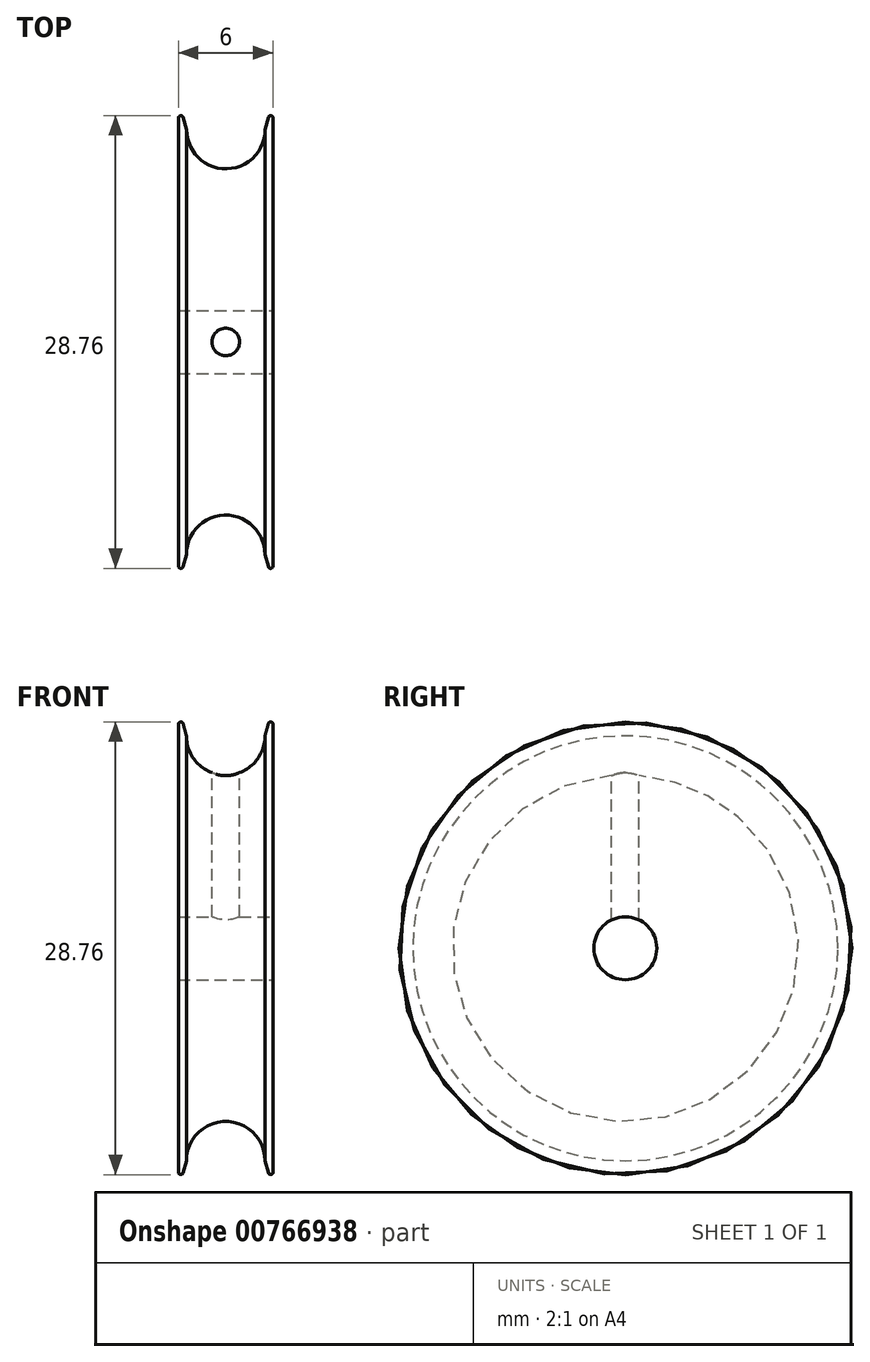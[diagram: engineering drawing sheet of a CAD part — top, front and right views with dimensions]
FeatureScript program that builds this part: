
annotation { "Feature Type Name" : "Feature", "Feature Type Description" : "" }
export const myFeature = defineFeature(function(context is Context, id is Id, definition is map)
    precondition{}
    {
        {
            var Q0;
            Q0=qCreatedBy(makeId("Front.planeOp"),FACE);
            var sketch = newSketch(context, id + "F0", { "sketchPlane" : qUnion([Q0])});
            skArc(sketch, "E0", {"start": v(-2.5, 13.5) * mm, "mid": v(0, 11) * mm, "end": v(2.5, 13.5) * mm});
            skLineSegment(sketch, "E1", {"start": v(2.5, 13.5) * mm, "end": v(2.5, 0) * mm, "construction": true});
            skLineSegment(sketch, "E2", {"start": v(-2.5, 13.5) * mm, "end": v(-2.5, 0) * mm, "construction": true});
            skLineSegment(sketch, "E3", {"start": v(2.5, 13.5) * mm, "end": v(3, 13.5) * mm, "construction": true});
            skLineSegment(sketch, "E4", {"start": v(3, 13.5) * mm, "end": v(3, 0) * mm});
            skLineSegment(sketch, "E5", {"start": v(-2.5, 13.5) * mm, "end": v(-3, 13.5) * mm, "construction": true});
            skLineSegment(sketch, "E6", {"start": v(-3, 13.5) * mm, "end": v(-3, 0) * mm});
            skLineSegment(sketch, "E7", {"start": v(-3, 0) * mm, "end": v(3, 0) * mm});
            skLineSegment(sketch, "E8", {"start": v(-2.5, 13.5) * mm, "end": v(-3, 15.37) * mm});
            skLineSegment(sketch, "E9", {"start": v(-3, 13.5) * mm, "end": v(-3, 15.37) * mm});
            skLineSegment(sketch, "E10.MirrorCS", {"start": v(2.5, 13.5) * mm, "end": v(3, 15.37) * mm});
            skLineSegment(sketch, "E11.MirrorCS", {"start": v(3, 13.5) * mm, "end": v(3, 15.37) * mm});
            skSolve(sketch);
        }
        {
            var Q0;
            Q0=makeQuery(id+"F0.imprint","IMPRINT",FACE,{"disambiguationData":[TD([[makeQuery(id+"F0.imprint","IMPRINT",EDGE,{"derivedFrom":sQuery(id+"F0.wireOp",EDGE,"E0")}),-1.0]])]});
            var Q1;
            Q1=sQuery(id+"F0.wireOp",EDGE,"E7");
            revolve(context, id + "F1", {"surfaceOperationType" : NewSurfaceOperationType.NEW, "entities" : qUnion([Q0]), "axis" : qUnion([Q1]), "revolveType" : RevolveType.FULL});
        }
        {
            var Q0;
            Q0=makeQuery(id+"F1.opRevolve","SWEPT_EDGE",EDGE,{"disambiguationData":[OSD([sQuery(id+"F0.wireOp",EDGE,"E8"),sQuery(id+"F0.wireOp",EDGE,"E9")])]});
            var Q1;
            Q1=makeQuery(id+"F1.opRevolve","SWEPT_EDGE",EDGE,{"disambiguationData":[OSD([sQuery(id+"F0.wireOp",EDGE,"E10.MirrorCS"),sQuery(id+"F0.wireOp",EDGE,"E11.MirrorCS")])]});
            fillet(context, id + "F2", {"entities" : qUnion([Q0, Q1]), "radius" : .15 * mm, "tangentPropagation" : true, "allowEdgeOverflow" : false});
        }
        {
            var Q0;
            Q0=makeQuery(id+"F1.opRevolve","SWEPT_FACE",FACE,{"disambiguationData":[OSD([sQuery(id+"F0.wireOp",EDGE,"E4")])]});
            var sketch = newSketch(context, id + "F3", { "sketchPlane" : qUnion([Q0])});
            skPoint(sketch, "E12", {"position": v(0, 0) * mm});
            skSolve(sketch);
        }
        {
            var Q0;
            Q0=sQuery(id+"F3.wireOp",VERTEX,"E12");
            var Q1;
            Q1=makeQuery(id+"F1.opRevolve","SWEPT_BODY",BODY,{"disambiguationData":[OSD([sQuery(id+"F0.wireOp",EDGE,"E0"),sQuery(id+"F0.wireOp",EDGE,"E3"),sQuery(id+"F0.wireOp",EDGE,"E4"),sQuery(id+"F0.wireOp",EDGE,"E5"),sQuery(id+"F0.wireOp",EDGE,"E6"),sQuery(id+"F0.wireOp",EDGE,"E7")])]});
            hole(context, id + "F4", {"style" : HoleStyle.SIMPLE, "endStyle" : HoleEndStyle.THROUGH, "holeDiameter" : 4 * mm, "majorDiameter" : 6.35 * mm, "isTappedThrough" : true, "tappedDepth" : 12.7 * mm, "tapClearance" : 3, "locations" : qUnion([Q0]), "scope" : qUnion([Q1])});
        }
        {
            var Q0;
            Q0=qCreatedBy(makeId("Top.planeOp"),FACE);
            cPlane(context, id + "F5", {"entities" : qUnion([Q0]), "cplaneType" : CPlaneType.OFFSET, "offset" : 12 * mm, "width" : 150 * mm, "height" : 150 * mm});
        }
        {
            var Q0;
            Q0=qCreatedBy(id+"F5.planeOp",FACE);
            var sketch = newSketch(context, id + "F6", { "sketchPlane" : qUnion([Q0])});
            skPoint(sketch, "E13", {"position": v(0, 0) * mm});
            skSolve(sketch);
        }
        {
            var Q0;
            Q0=sQuery(id+"F6.wireOp",VERTEX,"E13");
            var Q1;
            Q1=makeQuery(id+"F1.opRevolve","SWEPT_BODY",BODY,{"disambiguationData":[OSD([sQuery(id+"F0.wireOp",EDGE,"E0"),sQuery(id+"F0.wireOp",EDGE,"E4"),sQuery(id+"F0.wireOp",EDGE,"E6"),sQuery(id+"F0.wireOp",EDGE,"E7"),sQuery(id+"F0.wireOp",EDGE,"E8"),sQuery(id+"F0.wireOp",EDGE,"E9"),sQuery(id+"F0.wireOp",EDGE,"E10.MirrorCS"),sQuery(id+"F0.wireOp",EDGE,"E11.MirrorCS")])]});
            hole(context, id + "F7", {"style" : HoleStyle.SIMPLE, "endStyle" : HoleEndStyle.BLIND, "holeDiameter" : 1.75 * mm, "majorDiameter" : 5 * mm, "holeDepth" : 10 * mm, "isTappedThrough" : true, "tappedDepth" : 12 * mm, "tapClearance" : 3, "locations" : qUnion([Q0]), "scope" : qUnion([Q1])});
        }
    });
